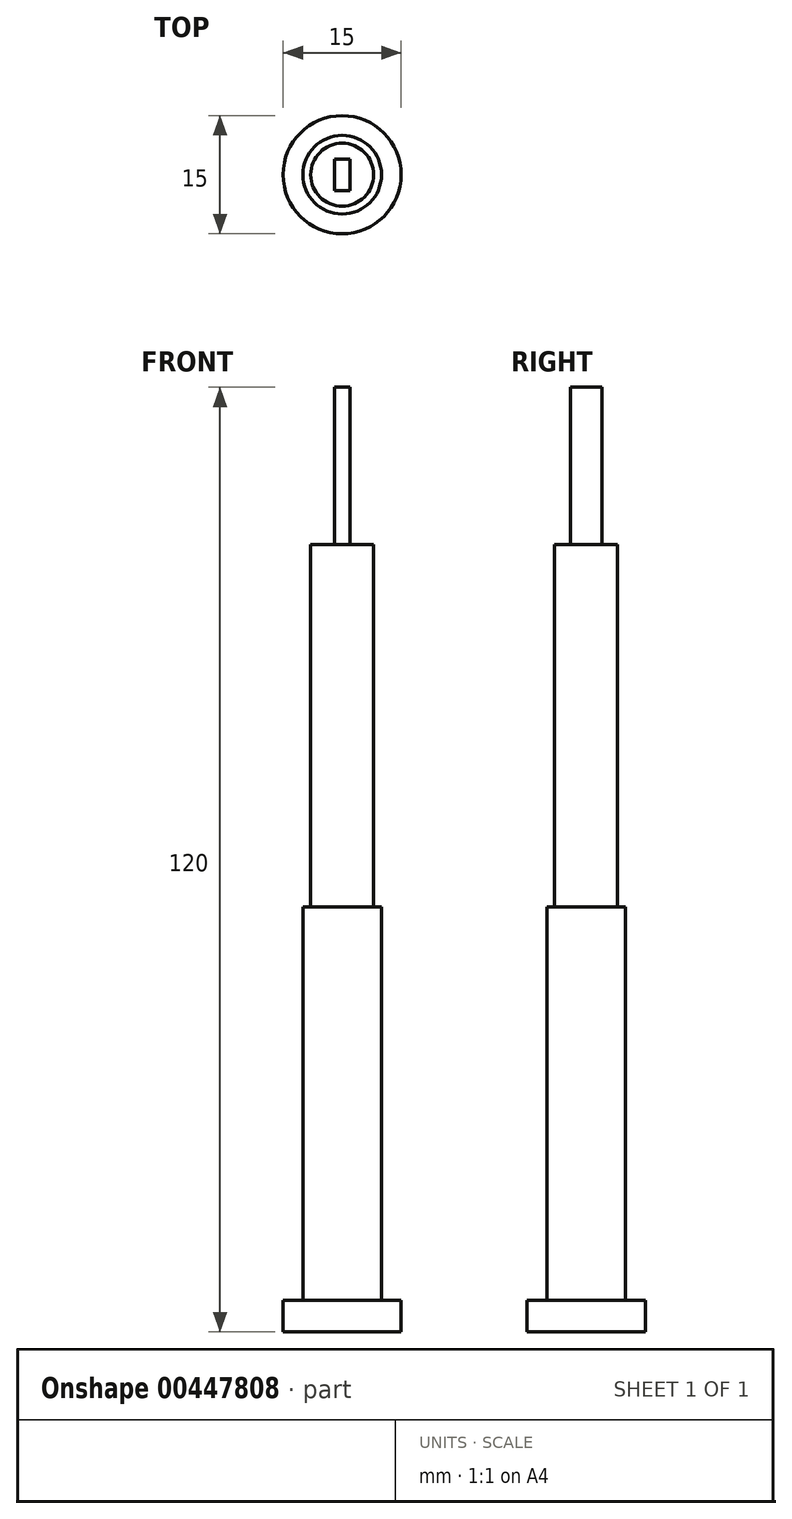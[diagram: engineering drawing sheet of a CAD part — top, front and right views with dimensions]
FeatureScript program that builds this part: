
annotation { "Feature Type Name" : "Feature", "Feature Type Description" : "" }
export const myFeature = defineFeature(function(context is Context, id is Id, definition is map)
    precondition{}
    {
        {
            var Q0;
            Q0=qCreatedBy(makeId("Top.planeOp"),FACE);
            var sketch = newSketch(context, id + "F0", { "sketchPlane" : qUnion([Q0])});
            skCircle(sketch, "E0", {"center": v(0, 0) * mm, "radius": 7.5 * mm});
            skSolve(sketch);
        }
        {
            var Q0;
            Q0=qSketchRegion(id+"F0",true);
            extrude(context, id + "F1", {"entities" : qUnion([Q0]), "depth" : 4 * mm});
        }
        {
            var Q0;
            Q0=qCreatedBy(makeId("Top.planeOp"),FACE);
            var sketch = newSketch(context, id + "F2", { "sketchPlane" : qUnion([Q0])});
            skCircle(sketch, "E1", {"center": v(0, 0) * mm, "radius": 5 * mm});
            skSolve(sketch);
        }
        {
            var Q0;
            Q0=qSketchRegion(id+"F2",true);
            extrude(context, id + "F3", {"entities" : qUnion([Q0]), "operationType" : NewBodyOperationType.ADD, "depth" : 54 * mm});
        }
        {
            var Q0;
            Q0=makeQuery(id+"F3.opExtrude","CAP_FACE",FACE,{"disambiguationData":[OSD([sQuery(id+"F2.wireOp",EDGE,"E1")])],"isStart":false});
            var sketch = newSketch(context, id + "F4", { "sketchPlane" : qUnion([Q0])});
            skCircle(sketch, "E2", {"center": v(0, 0) * mm, "radius": 4 * mm});
            skSolve(sketch);
        }
        {
            var Q0;
            Q0=qSketchRegion(id+"F4",true);
            extrude(context, id + "F5", {"entities" : qUnion([Q0]), "operationType" : NewBodyOperationType.ADD, "depth" : 46 * mm});
        }
        {
            var Q0;
            Q0=makeQuery(id+"F5.opExtrude","CAP_FACE",FACE,{"disambiguationData":[OSD([sQuery(id+"F4.wireOp",EDGE,"E2")])],"isStart":false});
            var sketch = newSketch(context, id + "F6", { "sketchPlane" : qUnion([Q0])});
            skLineSegment(sketch, "E3.bottom", {"start": v(-1, 2) * mm, "end": v(1, 2) * mm});
            skLineSegment(sketch, "E3.top", {"start": v(-1, -2) * mm, "end": v(1, -2) * mm});
            skLineSegment(sketch, "E3.left", {"start": v(-1, 2) * mm, "end": v(-1, -2) * mm});
            skLineSegment(sketch, "E3.right", {"start": v(1, 2) * mm, "end": v(1, -2) * mm});
            skSolve(sketch);
        }
        {
            var Q0;
            Q0=qSketchRegion(id+"F6",true);
            extrude(context, id + "F7", {"entities" : qUnion([Q0]), "operationType" : NewBodyOperationType.ADD, "depth" : 20 * mm});
        }
    });
